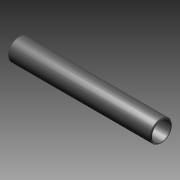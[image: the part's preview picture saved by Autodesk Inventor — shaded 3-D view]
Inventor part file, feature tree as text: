
AUTODESK INVENTOR PART (.ipt)
format: ipt  version: 2011 SP1 (Build 150282100, 282)  size: 122,368 bytes
history: native  units: in
note: dims shown in document units (in); Inventor stores cm internally (conversion verified against a paired STEP export)
features: other x42, revolve x1, sketch x1
ambient origin geometry x8: Origin, YZ Plane, XZ Plane, XY Plane, X Axis, Y Axis, Z Axis, Center Point
bodies: Solid1 (feature_tree)
feature tree (44):
  revolve  "Revolution1"  [1 undecoded]
  other  "cp1_XY"
  other  "cp1_YZ"
  other  "cp1_ZX"
  other  "cp1_X"
  other  "cp1_Y"
  other  "cp1_Z"
  other  "cp1_Center"
  other  "cp2_XY"
  other  "cp2_YZ"
  other  "cp2_ZX"
  other  "cp2_X"
  other  "cp2_Y"
  other  "cp2_Z"
  other  "cp2_Center"
  other  "cp3_XY"
  other  "cp3_YZ"
  other  "cp3_ZX"
  other  "cp3_X"
  other  "cp3_Y"
  other  "cp3_Z"
  other  "cp3_Center"
  other  "cp4_XY"
  other  "cp4_YZ"
  other  "cp4_ZX"
  other  "cp4_X"
  other  "cp4_Y"
  other  "cp4_Z"
  other  "cp4_Center"
  other  "tube_front_XY"
  other  "tube_front_YZ"
  other  "tube_front_ZX"
  other  "tube_front_X"
  other  "tube_front_Y"
  other  "tube_front_Z"
  other  "tube_front_Center"
  other  "tube_rear_XY"
  other  "tube_rear_YZ"
  other  "tube_rear_ZX"
  other  "tube_rear_X"
  other  "tube_rear_Y"
  other  "tube_rear_Z"
  other  "tube_rear_Center"
  sketch  "Sketch_1"  dims[d0=360.0deg]
note: 1 required parameter value undecoded (feature->parameter linkage not recoverable at this tier; creation-order binding heuristic only, values carry confidence <= 0.55)
